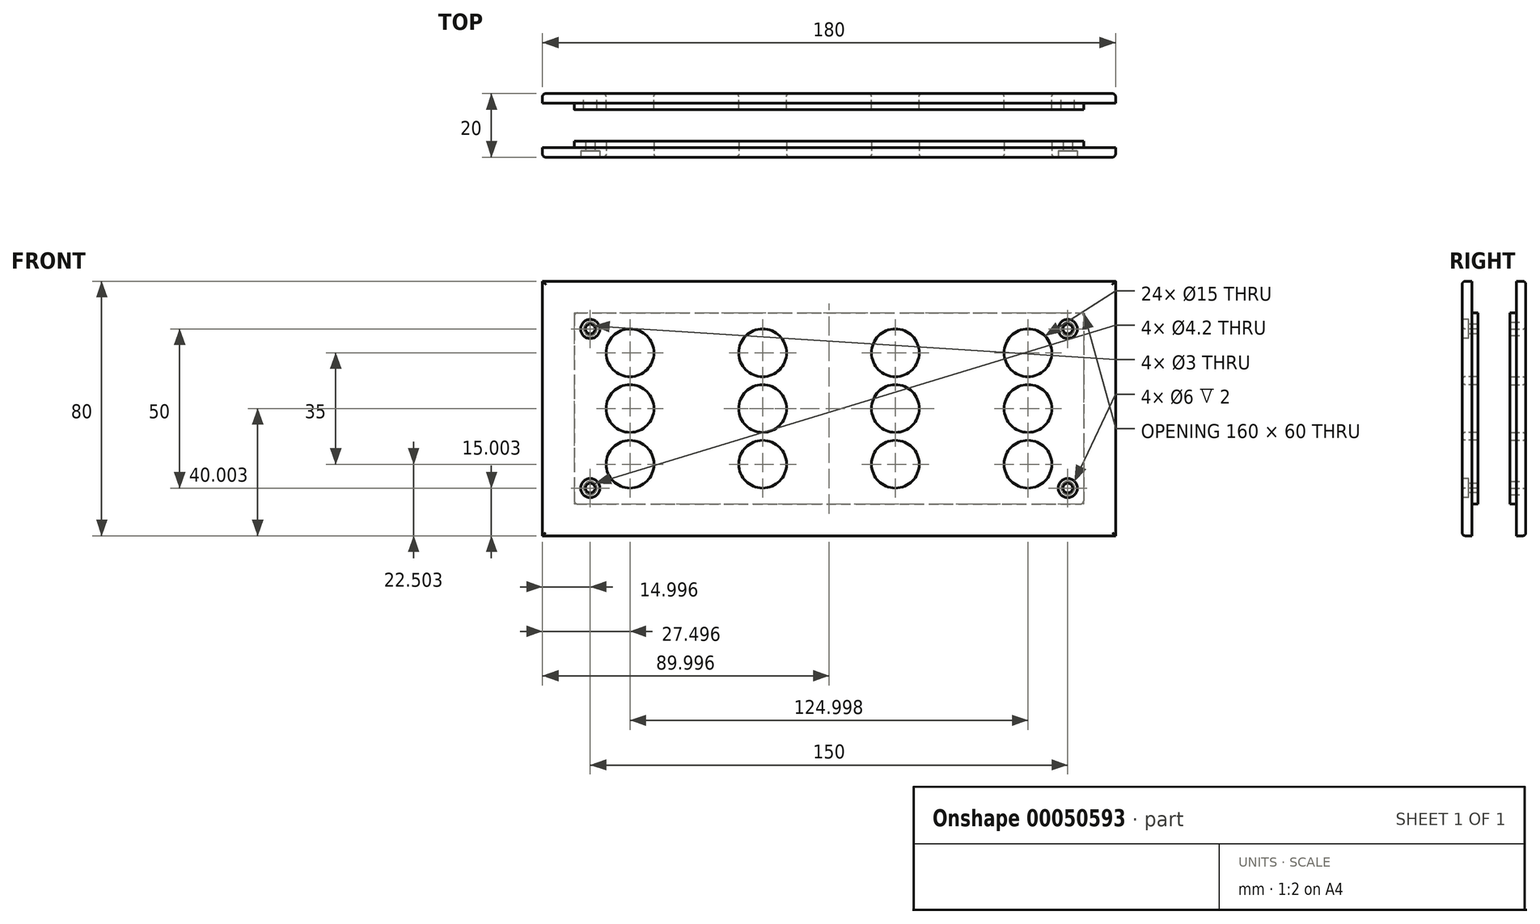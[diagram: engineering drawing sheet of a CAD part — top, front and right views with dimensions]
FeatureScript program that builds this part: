
annotation { "Feature Type Name" : "Feature", "Feature Type Description" : "" }
export const myFeature = defineFeature(function(context is Context, id is Id, definition is map)
    precondition{}
    {
        {
            var Q0;
            Q0=qCreatedBy(makeId("Front.planeOp"),FACE);
            var sketch = newSketch(context, id + "F0", { "sketchPlane" : qUnion([Q0])});
            skLineSegment(sketch, "E0.bottom", {"start": v(-94.58, -40.65) * mm, "end": v(65.42, -40.65) * mm});
            skLineSegment(sketch, "E0.top", {"start": v(-94.58, -100.65) * mm, "end": v(65.42, -100.65) * mm});
            skLineSegment(sketch, "E0.left", {"start": v(-94.58, -40.65) * mm, "end": v(-94.58, -100.65) * mm});
            skLineSegment(sketch, "E0.right", {"start": v(65.42, -40.65) * mm, "end": v(65.42, -100.65) * mm});
            skLineSegment(sketch, "E1.bottom", {"start": v(-104.58, -30.65) * mm, "end": v(75.42, -30.65) * mm});
            skLineSegment(sketch, "E1.top", {"start": v(-104.58, -110.65) * mm, "end": v(75.42, -110.65) * mm});
            skLineSegment(sketch, "E1.left", {"start": v(-104.58, -30.65) * mm, "end": v(-104.58, -110.65) * mm});
            skLineSegment(sketch, "E1.right", {"start": v(75.42, -30.65) * mm, "end": v(75.42, -110.65) * mm});
            skPoint(sketch, "E2", {"position": v(65.42, -70.65) * mm});
            skPoint(sketch, "E3", {"position": v(-14.58, -40.65) * mm});
            skSolve(sketch);
        }
        {
            var Q0;
            Q0=makeQuery(id+"F0.imprint","IMPRINT",FACE,{"disambiguationData":[TD([[makeQuery(id+"F0.imprint","IMPRINT",EDGE,{"derivedFrom":sQuery(id+"F0.wireOp",EDGE,"E0.bottom")}),1.0]])]});
            var sketch = newSketch(context, id + "F1", { "sketchPlane" : qUnion([Q0])});
            skCircle(sketch, "E4", {"center": v(-77.08, -53.15) * mm, "radius": 7.5 * mm});
            skLineSegment(sketch, "E5.bottom", {"start": v(-77.08, -53.15) * mm, "end": v(47.92, -53.15) * mm, "construction": true});
            skLineSegment(sketch, "E5.top", {"start": v(-77.08, -88.15) * mm, "end": v(47.92, -88.15) * mm, "construction": true});
            skLineSegment(sketch, "E5.left", {"start": v(-77.08, -53.15) * mm, "end": v(-77.08, -88.15) * mm, "construction": true});
            skLineSegment(sketch, "E5.right", {"start": v(47.92, -53.15) * mm, "end": v(47.92, -88.15) * mm, "construction": true});
            skPoint(sketch, "E6", {"position": v(47.92, -70.65) * mm});
            skPoint(sketch, "E7", {"position": v(-14.58, -53.15) * mm});
            skCircle(sketch, "E8.0.1.0", {"center": v(-77.08, -70.65) * mm, "radius": 7.5 * mm});
            skCircle(sketch, "E8.0.2.0", {"center": v(-77.08, -88.15) * mm, "radius": 7.5 * mm});
            skCircle(sketch, "E8.1.0.0", {"center": v(-35.42, -53.15) * mm, "radius": 7.5 * mm});
            skCircle(sketch, "E8.1.1.0", {"center": v(-35.42, -70.65) * mm, "radius": 7.5 * mm});
            skCircle(sketch, "E8.1.2.0", {"center": v(-35.42, -88.15) * mm, "radius": 7.5 * mm});
            skCircle(sketch, "E8.2.0.0", {"center": v(6.25, -53.15) * mm, "radius": 7.5 * mm});
            skCircle(sketch, "E8.2.1.0", {"center": v(6.25, -70.65) * mm, "radius": 7.5 * mm});
            skCircle(sketch, "E8.2.2.0", {"center": v(6.25, -88.15) * mm, "radius": 7.5 * mm});
            skCircle(sketch, "E8.3.0.0", {"center": v(47.91, -53.15) * mm, "radius": 7.5 * mm});
            skCircle(sketch, "E8.3.1.0", {"center": v(47.91, -70.65) * mm, "radius": 7.5 * mm});
            skCircle(sketch, "E8.3.2.0", {"center": v(47.91, -88.15) * mm, "radius": 7.5 * mm});
            skLineSegment(sketch, "E8.direction1", {"start": v(-77.08, -53.15) * mm, "end": v(-35.42, -53.15) * mm, "construction": true});
            skLineSegment(sketch, "E8.direction2", {"start": v(-77.08, -53.15) * mm, "end": v(-77.08, -70.65) * mm, "construction": true});
            skSolve(sketch);
        }
        {
            var Q0;
            Q0=makeQuery(id+"F0.imprint","IMPRINT",FACE,{"disambiguationData":[TD([[makeQuery(id+"F0.imprint","IMPRINT",EDGE,{"derivedFrom":sQuery(id+"F0.wireOp",EDGE,"E0.bottom")}),1.0]])]});
            extrude(context, id + "F2", {"entities" : qUnion([Q0]), "depth" : 3 * mm});
        }
        {
            var Q0;
            Q0=makeQuery(id+"F1.imprint","IMPRINT",FACE,{"disambiguationData":[TD([[makeQuery(id+"F1.imprint","IMPRINT",EDGE,{"derivedFrom":sQuery(id+"F1.wireOp",EDGE,"E4")}),-1.0]])]});
            extrude(context, id + "F3", {"entities" : qUnion([Q0]), "operationType" : NewBodyOperationType.ADD, "depth" : 5 * mm});
        }
        {
            var Q0;
            Q0=makeQuery(id+"F3.opExtrude","SWEPT_EDGE",EDGE,{"disambiguationData":[OSD([sQuery(id+"F0.wireOp",EDGE,"E0.bottom"),sQuery(id+"F0.wireOp",EDGE,"E0.right")])]});
            var Q1;
            Q1=makeQuery(id+"F3.opExtrude","SWEPT_EDGE",EDGE,{"disambiguationData":[OSD([sQuery(id+"F0.wireOp",EDGE,"E0.top"),sQuery(id+"F0.wireOp",EDGE,"E0.right")])]});
            var Q2;
            Q2=makeQuery(id+"F3.opExtrude","SWEPT_EDGE",EDGE,{"disambiguationData":[OSD([sQuery(id+"F0.wireOp",EDGE,"E0.top"),sQuery(id+"F0.wireOp",EDGE,"E0.left")])]});
            var Q3;
            Q3=makeQuery(id+"F3.opExtrude","SWEPT_EDGE",EDGE,{"disambiguationData":[OSD([sQuery(id+"F0.wireOp",EDGE,"E0.bottom"),sQuery(id+"F0.wireOp",EDGE,"E0.left")])]});
            fillet(context, id + "F4", {"entities" : qUnion([Q0, Q1, Q2, Q3]), "radius" : 1 * mm, "tangentPropagation" : true, "allowEdgeOverflow" : false});
        }
        {
            var Q0;
            {var subQ0=sQuery(id+"F0.wireOp",EDGE,"E0.right");var subQ1=sQuery(id+"F0.wireOp",EDGE,"E0.left");var subQ2=sQuery(id+"F0.wireOp",EDGE,"E0.top");var subQ3=sQuery(id+"F0.wireOp",EDGE,"E0.bottom");Q0=makeQuery(id+"F3.boolean.opBoolean","MERGE",FACE,{"derivedFrom":[makeQuery(id+"F2.opExtrude","CAP_FACE",FACE,{"disambiguationData":[OSD([subQ3,subQ2,subQ1,subQ0,sQuery(id+"F0.wireOp",EDGE,"E1.bottom"),sQuery(id+"F0.wireOp",EDGE,"E1.top"),sQuery(id+"F0.wireOp",EDGE,"E1.left"),sQuery(id+"F0.wireOp",EDGE,"E1.right")])],"isStart":true}),makeQuery(id+"F3.opExtrude","CAP_FACE",FACE,{"disambiguationData":[OSD([subQ3,subQ2,subQ1,subQ0,sQuery(id+"F1.wireOp",EDGE,"E4"),sQuery(id+"F1.wireOp",EDGE,"E8.0.1.0"),sQuery(id+"F1.wireOp",EDGE,"E8.0.2.0"),sQuery(id+"F1.wireOp",EDGE,"E8.1.0.0"),sQuery(id+"F1.wireOp",EDGE,"E8.1.1.0"),sQuery(id+"F1.wireOp",EDGE,"E8.1.2.0"),sQuery(id+"F1.wireOp",EDGE,"E8.2.0.0"),sQuery(id+"F1.wireOp",EDGE,"E8.2.1.0"),sQuery(id+"F1.wireOp",EDGE,"E8.2.2.0"),sQuery(id+"F1.wireOp",EDGE,"E8.3.0.0"),sQuery(id+"F1.wireOp",EDGE,"E8.3.1.0"),sQuery(id+"F1.wireOp",EDGE,"E8.3.2.0")])],"isStart":true})]});}
            fillet(context, id + "F5", {"entities" : qUnion([Q0]), "radius" : 1 * mm, "tangentPropagation" : true, "allowEdgeOverflow" : false});
        }
        {
            var Q0;
            {var subQ0=sQuery(id+"F0.wireOp",EDGE,"E0.right");var subQ1=sQuery(id+"F0.wireOp",EDGE,"E0.left");var subQ2=sQuery(id+"F0.wireOp",EDGE,"E0.top");var subQ3=sQuery(id+"F0.wireOp",EDGE,"E0.bottom");Q0=makeQuery(id+"F3.boolean.opBoolean","MERGE",FACE,{"derivedFrom":[makeQuery(id+"F2.opExtrude","CAP_FACE",FACE,{"disambiguationData":[OSD([subQ3,subQ2,subQ1,subQ0,sQuery(id+"F0.wireOp",EDGE,"E1.bottom"),sQuery(id+"F0.wireOp",EDGE,"E1.top"),sQuery(id+"F0.wireOp",EDGE,"E1.left"),sQuery(id+"F0.wireOp",EDGE,"E1.right")])],"isStart":true}),makeQuery(id+"F3.opExtrude","CAP_FACE",FACE,{"disambiguationData":[OSD([subQ3,subQ2,subQ1,subQ0,sQuery(id+"F1.wireOp",EDGE,"E4"),sQuery(id+"F1.wireOp",EDGE,"E8.0.1.0"),sQuery(id+"F1.wireOp",EDGE,"E8.0.2.0"),sQuery(id+"F1.wireOp",EDGE,"E8.1.0.0"),sQuery(id+"F1.wireOp",EDGE,"E8.1.1.0"),sQuery(id+"F1.wireOp",EDGE,"E8.1.2.0"),sQuery(id+"F1.wireOp",EDGE,"E8.2.0.0"),sQuery(id+"F1.wireOp",EDGE,"E8.2.1.0"),sQuery(id+"F1.wireOp",EDGE,"E8.2.2.0"),sQuery(id+"F1.wireOp",EDGE,"E8.3.0.0"),sQuery(id+"F1.wireOp",EDGE,"E8.3.1.0"),sQuery(id+"F1.wireOp",EDGE,"E8.3.2.0")])],"isStart":true})]});}
            var sketch = newSketch(context, id + "F6", { "sketchPlane" : qUnion([Q0])});
            skLineSegment(sketch, "E9.bottom", {"start": v(-65.42, -40.65) * mm, "end": v(94.58, -40.65) * mm, "construction": true});
            skLineSegment(sketch, "E9.top", {"start": v(-65.42, -100.65) * mm, "end": v(94.58, -100.65) * mm, "construction": true});
            skLineSegment(sketch, "E9.left", {"start": v(-65.42, -40.65) * mm, "end": v(-65.42, -100.65) * mm, "construction": true});
            skLineSegment(sketch, "E9.right", {"start": v(94.58, -40.65) * mm, "end": v(94.58, -100.65) * mm, "construction": true});
            skPoint(sketch, "E10", {"position": v(-60.42, -45.65) * mm});
            skCircle(sketch, "E11", {"center": v(-60.42, -45.65) * mm, "radius": 1.5 * mm});
            skPoint(sketch, "E12", {"position": v(14.58, -40.65) * mm});
            skPoint(sketch, "E13", {"position": v(14.58, -100.65) * mm});
            skLineSegment(sketch, "E14", {"start": v(14.58, -40.65) * mm, "end": v(14.58, -100.65) * mm, "construction": true});
            skPoint(sketch, "E15", {"position": v(-65.42, -70.65) * mm});
            skPoint(sketch, "E16", {"position": v(94.58, -70.65) * mm});
            skLineSegment(sketch, "E17", {"start": v(-65.42, -70.65) * mm, "end": v(94.58, -70.65) * mm, "construction": true});
            skCircle(sketch, "E18.MirrorC", {"center": v(89.58, -45.65) * mm, "radius": 1.5 * mm});
            skCircle(sketch, "E19.MirrorC", {"center": v(-60.42, -95.65) * mm, "radius": 1.5 * mm});
            skCircle(sketch, "E20.MirrorC", {"center": v(89.58, -95.65) * mm, "radius": 1.5 * mm});
            skSolve(sketch);
        }
        {
            var Q0;
            Q0 = qSketchRegion(id + "F6", true);
            extrude(context, id + "F7", {"entities" : qUnion([Q0]), "operationType" : NewBodyOperationType.REMOVE, "endBound" : BoundingType.THROUGH_ALL, "oppositeDirection" : true, "depth" : 25 * mm});
        }
        {
            var Q0;
            Q0=makeQuery(id+"F3.opExtrude","CAP_FACE",FACE,{"disambiguationData":[OSD([sQuery(id+"F0.wireOp",EDGE,"E0.bottom"),sQuery(id+"F0.wireOp",EDGE,"E0.top"),sQuery(id+"F0.wireOp",EDGE,"E0.left"),sQuery(id+"F0.wireOp",EDGE,"E0.right"),sQuery(id+"F1.wireOp",EDGE,"E4"),sQuery(id+"F1.wireOp",EDGE,"E8.0.1.0"),sQuery(id+"F1.wireOp",EDGE,"E8.0.2.0"),sQuery(id+"F1.wireOp",EDGE,"E8.1.0.0"),sQuery(id+"F1.wireOp",EDGE,"E8.1.1.0"),sQuery(id+"F1.wireOp",EDGE,"E8.1.2.0"),sQuery(id+"F1.wireOp",EDGE,"E8.2.0.0"),sQuery(id+"F1.wireOp",EDGE,"E8.2.1.0"),sQuery(id+"F1.wireOp",EDGE,"E8.2.2.0"),sQuery(id+"F1.wireOp",EDGE,"E8.3.0.0"),sQuery(id+"F1.wireOp",EDGE,"E8.3.1.0"),sQuery(id+"F1.wireOp",EDGE,"E8.3.2.0")])],"isStart":false});
            cPlane(context, id + "F8", {"entities" : qUnion([Q0]), "cplaneType" : CPlaneType.OFFSET, "offset" : 5 * mm, "width" : 150 * mm, "height" : 150 * mm});
        }
        {
            var Q0;
            Q0=makeQuery(id+"F2.opExtrude","SWEPT_BODY",BODY,{"disambiguationData":[OSD([sQuery(id+"F0.wireOp",EDGE,"E0.bottom"),sQuery(id+"F0.wireOp",EDGE,"E0.top"),sQuery(id+"F0.wireOp",EDGE,"E0.left"),sQuery(id+"F0.wireOp",EDGE,"E0.right"),sQuery(id+"F0.wireOp",EDGE,"E1.bottom"),sQuery(id+"F0.wireOp",EDGE,"E1.top"),sQuery(id+"F0.wireOp",EDGE,"E1.left"),sQuery(id+"F0.wireOp",EDGE,"E1.right")])]});
            var Q1;
            Q1=qCreatedBy(id+"F8.planeOp",FACE);
            mirror(context, id + "F9", {"entities" : qUnion([Q0]), "mirrorPlane" : qUnion([Q1])});
        }
        {
            var Q0;
            {var subQ0=sQuery(id+"F0.wireOp",EDGE,"E0.right");var subQ1=sQuery(id+"F0.wireOp",EDGE,"E0.left");var subQ2=sQuery(id+"F0.wireOp",EDGE,"E0.top");var subQ3=sQuery(id+"F0.wireOp",EDGE,"E0.bottom");Q0=makeQuery(id+"F3.boolean.opBoolean","MERGE",FACE,{"derivedFrom":[makeQuery(id+"F2.opExtrude","CAP_FACE",FACE,{"disambiguationData":[OSD([subQ3,subQ2,subQ1,subQ0,sQuery(id+"F0.wireOp",EDGE,"E1.bottom"),sQuery(id+"F0.wireOp",EDGE,"E1.top"),sQuery(id+"F0.wireOp",EDGE,"E1.left"),sQuery(id+"F0.wireOp",EDGE,"E1.right")])],"isStart":true}),makeQuery(id+"F3.opExtrude","CAP_FACE",FACE,{"disambiguationData":[OSD([subQ3,subQ2,subQ1,subQ0,sQuery(id+"F1.wireOp",EDGE,"E4"),sQuery(id+"F1.wireOp",EDGE,"E8.0.1.0"),sQuery(id+"F1.wireOp",EDGE,"E8.0.2.0"),sQuery(id+"F1.wireOp",EDGE,"E8.1.0.0"),sQuery(id+"F1.wireOp",EDGE,"E8.1.1.0"),sQuery(id+"F1.wireOp",EDGE,"E8.1.2.0"),sQuery(id+"F1.wireOp",EDGE,"E8.2.0.0"),sQuery(id+"F1.wireOp",EDGE,"E8.2.1.0"),sQuery(id+"F1.wireOp",EDGE,"E8.2.2.0"),sQuery(id+"F1.wireOp",EDGE,"E8.3.0.0"),sQuery(id+"F1.wireOp",EDGE,"E8.3.1.0"),sQuery(id+"F1.wireOp",EDGE,"E8.3.2.0")])],"isStart":true})]});}
            var sketch = newSketch(context, id + "F10", { "sketchPlane" : qUnion([Q0])});
            skPoint(sketch, "E21", {"position": v(-60.42, -45.65) * mm});
            skPoint(sketch, "E22", {"position": v(-60.42, -95.65) * mm});
            skPoint(sketch, "E23", {"position": v(89.58, -95.65) * mm});
            skPoint(sketch, "E24", {"position": v(89.58, -45.65) * mm});
            skCircle(sketch, "E25", {"center": v(-60.42, -45.65) * mm, "radius": 2.1 * mm});
            skLineSegment(sketch, "E26", {"start": v(14.58, -40.65) * mm, "end": v(14.58, -100.65) * mm, "construction": true});
            skLineSegment(sketch, "E27", {"start": v(-65.42, -70.65) * mm, "end": v(94.58, -70.65) * mm, "construction": true});
            skCircle(sketch, "E28.MirrorC", {"center": v(89.58, -45.65) * mm, "radius": 2.1 * mm});
            skCircle(sketch, "E29.MirrorC", {"center": v(-60.42, -95.65) * mm, "radius": 2.1 * mm});
            skCircle(sketch, "E30.MirrorC", {"center": v(89.58, -95.65) * mm, "radius": 2.1 * mm});
            skSolve(sketch);
        }
        {
            var Q0;
            Q0 = qSketchRegion(id + "F10", true);
            var Q1;
            Q1=makeQuery(id+"F3.opExtrude","CAP_FACE",FACE,{"disambiguationData":[OSD([sQuery(id+"F0.wireOp",EDGE,"E0.bottom"),sQuery(id+"F0.wireOp",EDGE,"E0.top"),sQuery(id+"F0.wireOp",EDGE,"E0.left"),sQuery(id+"F0.wireOp",EDGE,"E0.right"),sQuery(id+"F1.wireOp",EDGE,"E4"),sQuery(id+"F1.wireOp",EDGE,"E8.0.1.0"),sQuery(id+"F1.wireOp",EDGE,"E8.0.2.0"),sQuery(id+"F1.wireOp",EDGE,"E8.1.0.0"),sQuery(id+"F1.wireOp",EDGE,"E8.1.1.0"),sQuery(id+"F1.wireOp",EDGE,"E8.1.2.0"),sQuery(id+"F1.wireOp",EDGE,"E8.2.0.0"),sQuery(id+"F1.wireOp",EDGE,"E8.2.1.0"),sQuery(id+"F1.wireOp",EDGE,"E8.2.2.0"),sQuery(id+"F1.wireOp",EDGE,"E8.3.0.0"),sQuery(id+"F1.wireOp",EDGE,"E8.3.1.0"),sQuery(id+"F1.wireOp",EDGE,"E8.3.2.0")])],"isStart":false});
            extrude(context, id + "F11", {"entities" : qUnion([Q0]), "operationType" : NewBodyOperationType.REMOVE, "endBound" : BoundingType.UP_TO_SURFACE, "oppositeDirection" : true, "endBoundEntityFace" : qUnion([Q1]), "depth" : 25 * mm});
        }
        {
            var Q0;
            {var subQ0=sQuery(id+"F0.wireOp",EDGE,"E0.right");var subQ1=sQuery(id+"F0.wireOp",EDGE,"E0.left");var subQ2=sQuery(id+"F0.wireOp",EDGE,"E0.top");var subQ3=sQuery(id+"F0.wireOp",EDGE,"E0.bottom");Q0=makeQuery(id+"F9.opPattern","COPY",FACE,{"derivedFrom":makeQuery(id+"F3.boolean.opBoolean","MERGE",FACE,{"derivedFrom":[makeQuery(id+"F2.opExtrude","CAP_FACE",FACE,{"disambiguationData":[OSD([subQ3,subQ2,subQ1,subQ0,sQuery(id+"F0.wireOp",EDGE,"E1.bottom"),sQuery(id+"F0.wireOp",EDGE,"E1.top"),sQuery(id+"F0.wireOp",EDGE,"E1.left"),sQuery(id+"F0.wireOp",EDGE,"E1.right")])],"isStart":true}),makeQuery(id+"F3.opExtrude","CAP_FACE",FACE,{"disambiguationData":[OSD([subQ3,subQ2,subQ1,subQ0,sQuery(id+"F1.wireOp",EDGE,"E4"),sQuery(id+"F1.wireOp",EDGE,"E8.0.1.0"),sQuery(id+"F1.wireOp",EDGE,"E8.0.2.0"),sQuery(id+"F1.wireOp",EDGE,"E8.1.0.0"),sQuery(id+"F1.wireOp",EDGE,"E8.1.1.0"),sQuery(id+"F1.wireOp",EDGE,"E8.1.2.0"),sQuery(id+"F1.wireOp",EDGE,"E8.2.0.0"),sQuery(id+"F1.wireOp",EDGE,"E8.2.1.0"),sQuery(id+"F1.wireOp",EDGE,"E8.2.2.0"),sQuery(id+"F1.wireOp",EDGE,"E8.3.0.0"),sQuery(id+"F1.wireOp",EDGE,"E8.3.1.0"),sQuery(id+"F1.wireOp",EDGE,"E8.3.2.0")])],"isStart":true})]}),"instanceName":"1"});}
            var sketch = newSketch(context, id + "F12", { "sketchPlane" : qUnion([Q0])});
            skLineSegment(sketch, "E31", {"start": v(-14.58, -40.65) * mm, "end": v(-14.58, -100.65) * mm, "construction": true});
            skLineSegment(sketch, "E32", {"start": v(-94.58, -70.65) * mm, "end": v(65.42, -70.65) * mm, "construction": true});
            skPoint(sketch, "E33", {"position": v(-89.58, -45.65) * mm});
            skCircle(sketch, "E34", {"center": v(-89.58, -45.65) * mm, "radius": 3 * mm});
            skCircle(sketch, "E35.MirrorC", {"center": v(60.42, -45.65) * mm, "radius": 3 * mm});
            skLineSegment(sketch, "E36.MirrorCS", {"start": v(65.42, -70.65) * mm, "end": v(-94.58, -70.65) * mm, "construction": true});
            skCircle(sketch, "E37.MirrorC", {"center": v(-89.58, -95.65) * mm, "radius": 3 * mm});
            skCircle(sketch, "E38.MirrorC", {"center": v(60.42, -95.65) * mm, "radius": 3 * mm});
            skSolve(sketch);
        }
        {
            var Q0;
            Q0 = qSketchRegion(id + "F12", true);
            extrude(context, id + "F13", {"entities" : qUnion([Q0]), "operationType" : NewBodyOperationType.REMOVE, "oppositeDirection" : true, "depth" : 2 * mm});
        }
    });
